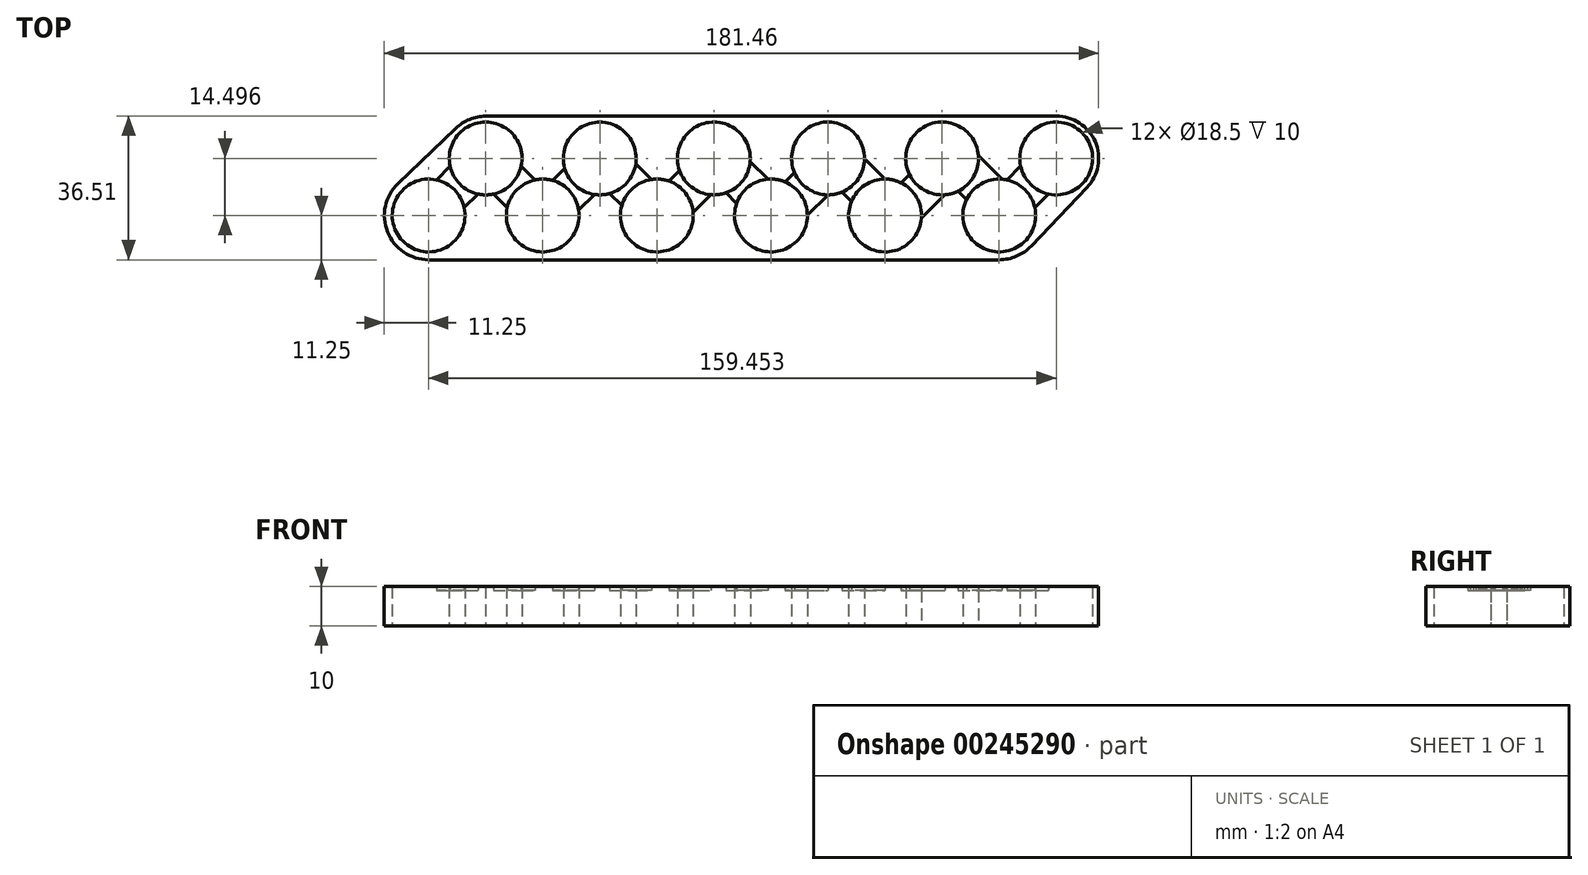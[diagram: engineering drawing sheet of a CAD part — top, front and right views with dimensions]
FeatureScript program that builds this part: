
annotation { "Feature Type Name" : "Feature", "Feature Type Description" : "" }
export const myFeature = defineFeature(function(context is Context, id is Id, definition is map)
    precondition{}
    {
        {
            var Q0;
            Q0=qCreatedBy(makeId("Top.planeOp"),FACE);
            var sketch = newSketch(context, id + "F0", { "sketchPlane" : qUnion([Q0])});
            skCircle(sketch, "E0", {"center": v(0, 0) * mm, "radius": 9.25 * mm});
            skCircle(sketch, "E1", {"center": v(14.5, 14.5) * mm, "radius": 9.25 * mm});
            skLineSegment(sketch, "E2", {"start": v(0, 0) * mm, "end": v(14.5, 0) * mm, "construction": true});
            skLineSegment(sketch, "E3", {"start": v(14.5, 0) * mm, "end": v(14.5, 14.5) * mm, "construction": true});
            skArc(sketch, "E4", {"start": v(-7.77, 8.14) * mm, "mid": v(-10.44, -4.19) * mm, "end": v(0, -11.25) * mm});
            skCircle(sketch, "E5.1.0.0", {"center": v(29, 0) * mm, "radius": 9.25 * mm});
            skCircle(sketch, "E5.1.0.3", {"center": v(43.49, 14.5) * mm, "radius": 9.25 * mm});
            skCircle(sketch, "E5.2.0.0", {"center": v(57.98, 0) * mm, "radius": 9.25 * mm});
            skCircle(sketch, "E5.2.0.3", {"center": v(72.48, 14.5) * mm, "radius": 9.25 * mm});
            skCircle(sketch, "E5.3.0.0", {"center": v(86.97, 0) * mm, "radius": 9.25 * mm});
            skCircle(sketch, "E5.3.0.3", {"center": v(101.47, 14.5) * mm, "radius": 9.25 * mm});
            skCircle(sketch, "E5.4.0.0", {"center": v(115.97, 0) * mm, "radius": 9.25 * mm});
            skCircle(sketch, "E5.4.0.3", {"center": v(130.46, 14.5) * mm, "radius": 9.25 * mm});
            skCircle(sketch, "E5.5.0.0", {"center": v(144.96, 0) * mm, "radius": 9.25 * mm});
            skArc(sketch, "E5.5.0.1", {"start": v(144.96, -11.25) * mm, "mid": v(149.39, -10.34) * mm, "end": v(153.1, -7.76) * mm});
            skArc(sketch, "E5.5.0.2", {"start": v(167.24, 7.07) * mm, "mid": v(169.34, 18.73) * mm, "end": v(159.45, 25.26) * mm});
            skCircle(sketch, "E5.5.0.3", {"center": v(159.45, 14.5) * mm, "radius": 9.25 * mm});
            skLineSegment(sketch, "E5.direction1", {"start": v(0, 0) * mm, "end": v(29, 0) * mm, "construction": true});
            skArc(sketch, "E6.trimOffspring", {"start": v(14.5, 25.26) * mm, "mid": v(10.4, 24.42) * mm, "end": v(6.9, 22.14) * mm});
            skLineSegment(sketch, "E7", {"start": v(0, -11.25) * mm, "end": v(144.96, -11.25) * mm});
            skLineSegment(sketch, "E8", {"start": v(14.5, 14.5) * mm, "end": v(14.5, 25.26) * mm, "construction": true});
            skLineSegment(sketch, "E9", {"start": v(159.45, 14.5) * mm, "end": v(159.45, 25.26) * mm, "construction": true});
            skLineSegment(sketch, "E10", {"start": v(159.45, 25.26) * mm, "end": v(14.5, 25.26) * mm});
            skLineSegment(sketch, "E11", {"start": v(153.1, -7.76) * mm, "end": v(167.24, 7.07) * mm});
            skLineSegment(sketch, "E12", {"start": v(-7.77, 8.14) * mm, "end": v(6.9, 22.14) * mm});
            skSolve(sketch);
        }
        {
            var Q0;
            Q0=makeQuery(id+"F0.imprint","IMPRINT",FACE,{"disambiguationData":[TD([[makeQuery(id+"F0.imprint","IMPRINT",EDGE,{"derivedFrom":sQuery(id+"F0.wireOp",EDGE,"E0")}),-1.0]])]});
            extrude(context, id + "F1", {"entities" : qUnion([Q0]), "depth" : 10 * mm});
        }
        {
            var Q0;
            Q0=makeQuery(id+"F1.opExtrude","CAP_FACE",FACE,{"disambiguationData":[OSD([sQuery(id+"F0.wireOp",EDGE,"E0"),sQuery(id+"F0.wireOp",EDGE,"E1"),sQuery(id+"F0.wireOp",EDGE,"E4"),sQuery(id+"F0.wireOp",EDGE,"E5.1.0.0"),sQuery(id+"F0.wireOp",EDGE,"E5.1.0.3"),sQuery(id+"F0.wireOp",EDGE,"E5.2.0.0"),sQuery(id+"F0.wireOp",EDGE,"E5.2.0.3"),sQuery(id+"F0.wireOp",EDGE,"E5.3.0.0"),sQuery(id+"F0.wireOp",EDGE,"E5.3.0.3"),sQuery(id+"F0.wireOp",EDGE,"E5.4.0.0"),sQuery(id+"F0.wireOp",EDGE,"E5.4.0.3"),sQuery(id+"F0.wireOp",EDGE,"E5.5.0.0"),sQuery(id+"F0.wireOp",EDGE,"E5.5.0.1"),sQuery(id+"F0.wireOp",EDGE,"E5.5.0.2"),sQuery(id+"F0.wireOp",EDGE,"E5.5.0.3"),sQuery(id+"F0.wireOp",EDGE,"E6.trimOffspring"),sQuery(id+"F0.wireOp",EDGE,"E7"),sQuery(id+"F0.wireOp",EDGE,"E10")])],"isStart":false});
            var sketch = newSketch(context, id + "F2", { "sketchPlane" : qUnion([Q0])});
            skLineSegment(sketch, "E13", {"start": v(0, 0) * mm, "end": v(14.5, 14.5) * mm, "construction": true});
            skLineSegment(sketch, "E14", {"start": v(14.5, 14.5) * mm, "end": v(29, 0) * mm, "construction": true});
            skLineSegment(sketch, "E15.0", {"start": v(3.18, -3.89) * mm, "end": v(14.5, 7.42) * mm});
            skLineSegment(sketch, "E16.0", {"start": v(17.85, 18.2) * mm, "end": v(32.7, 3.36) * mm});
            skLineSegment(sketch, "E17.0", {"start": v(-3.89, 3.18) * mm, "end": v(10.96, 18.03) * mm});
            skLineSegment(sketch, "E18.0", {"start": v(14.5, 7.42) * mm, "end": v(25.63, -3.71) * mm});
            skLineSegment(sketch, "E19", {"start": v(-3.89, 3.18) * mm, "end": v(3.18, -3.89) * mm});
            skLineSegment(sketch, "E20", {"start": v(25.63, -3.71) * mm, "end": v(32.7, 3.36) * mm});
            skLineSegment(sketch, "E21", {"start": v(17.85, 18.2) * mm, "end": v(10.96, 18.03) * mm});
            skLineSegment(sketch, "E22.1.0.0", {"start": v(25.8, 3.18) * mm, "end": v(40.66, 18.03) * mm});
            skLineSegment(sketch, "E22.1.0.1", {"start": v(25.8, 3.18) * mm, "end": v(32.88, -3.89) * mm});
            skLineSegment(sketch, "E22.1.0.2", {"start": v(32.88, -3.89) * mm, "end": v(44.2, 7.42) * mm});
            skLineSegment(sketch, "E22.1.0.3", {"start": v(44.2, 7.42) * mm, "end": v(55.33, -3.71) * mm});
            skLineSegment(sketch, "E22.1.0.4", {"start": v(55.33, -3.71) * mm, "end": v(62.4, 3.36) * mm});
            skLineSegment(sketch, "E22.1.0.5", {"start": v(47.55, 18.2) * mm, "end": v(62.4, 3.36) * mm});
            skLineSegment(sketch, "E22.1.0.6", {"start": v(47.55, 18.2) * mm, "end": v(40.66, 18.03) * mm});
            skLineSegment(sketch, "E22.2.0.0", {"start": v(55.5, 3.18) * mm, "end": v(70.36, 18.03) * mm});
            skLineSegment(sketch, "E22.2.0.1", {"start": v(55.5, 3.18) * mm, "end": v(62.58, -3.89) * mm});
            skLineSegment(sketch, "E22.2.0.2", {"start": v(62.58, -3.89) * mm, "end": v(73.9, 7.42) * mm});
            skLineSegment(sketch, "E22.2.0.3", {"start": v(73.9, 7.42) * mm, "end": v(85.03, -3.71) * mm});
            skLineSegment(sketch, "E22.2.0.4", {"start": v(85.03, -3.71) * mm, "end": v(92.1, 3.36) * mm});
            skLineSegment(sketch, "E22.2.0.5", {"start": v(77.25, 18.2) * mm, "end": v(92.1, 3.36) * mm});
            skLineSegment(sketch, "E22.2.0.6", {"start": v(77.25, 18.2) * mm, "end": v(70.36, 18.03) * mm});
            skLineSegment(sketch, "E22.3.0.0", {"start": v(85.2, 3.18) * mm, "end": v(100.06, 18.03) * mm});
            skLineSegment(sketch, "E22.3.0.1", {"start": v(85.2, 3.18) * mm, "end": v(92.28, -3.89) * mm});
            skLineSegment(sketch, "E22.3.0.2", {"start": v(92.28, -3.89) * mm, "end": v(103.6, 7.42) * mm});
            skLineSegment(sketch, "E22.3.0.3", {"start": v(103.6, 7.42) * mm, "end": v(114.73, -3.71) * mm});
            skLineSegment(sketch, "E22.3.0.4", {"start": v(114.73, -3.71) * mm, "end": v(121.8, 3.36) * mm});
            skLineSegment(sketch, "E22.3.0.5", {"start": v(106.95, 18.2) * mm, "end": v(121.8, 3.36) * mm});
            skLineSegment(sketch, "E22.3.0.6", {"start": v(106.95, 18.2) * mm, "end": v(100.06, 18.03) * mm});
            skLineSegment(sketch, "E22.4.0.0", {"start": v(114.9, 3.18) * mm, "end": v(129.75, 18.03) * mm});
            skLineSegment(sketch, "E22.4.0.1", {"start": v(114.9, 3.18) * mm, "end": v(121.98, -3.89) * mm});
            skLineSegment(sketch, "E22.4.0.2", {"start": v(121.98, -3.89) * mm, "end": v(133.29, 7.42) * mm});
            skLineSegment(sketch, "E22.4.0.3", {"start": v(133.29, 7.42) * mm, "end": v(144.43, -3.71) * mm});
            skLineSegment(sketch, "E22.4.0.4", {"start": v(144.43, -3.71) * mm, "end": v(151.5, 3.36) * mm});
            skLineSegment(sketch, "E22.4.0.5", {"start": v(136.65, 18.2) * mm, "end": v(151.5, 3.36) * mm});
            skLineSegment(sketch, "E22.4.0.6", {"start": v(136.65, 18.2) * mm, "end": v(129.75, 18.03) * mm});
            skLineSegment(sketch, "E22.direction1", {"start": v(-3.89, 3.18) * mm, "end": v(25.8, 3.18) * mm, "construction": true});
            skLineSegment(sketch, "E23", {"start": v(144.96, 0) * mm, "end": v(159.45, 14.5) * mm, "construction": true});
            skLineSegment(sketch, "E24.0", {"start": v(141.24, 3.36) * mm, "end": v(156.1, 18.2) * mm});
            skLineSegment(sketch, "E25.0", {"start": v(148.32, -3.71) * mm, "end": v(163.16, 11.14) * mm});
            skLineSegment(sketch, "E26", {"start": v(156.1, 18.2) * mm, "end": v(163.16, 11.14) * mm});
            skLineSegment(sketch, "E27", {"start": v(141.24, 3.36) * mm, "end": v(148.32, -3.71) * mm});
            skSolve(sketch);
        }
        {
            var Q0;
            Q0 = qSketchRegion(id + "F2", true);
            extrude(context, id + "F3", {"entities" : qUnion([Q0]), "operationType" : NewBodyOperationType.REMOVE, "oppositeDirection" : true, "depth" : 1 * mm});
        }
    });
